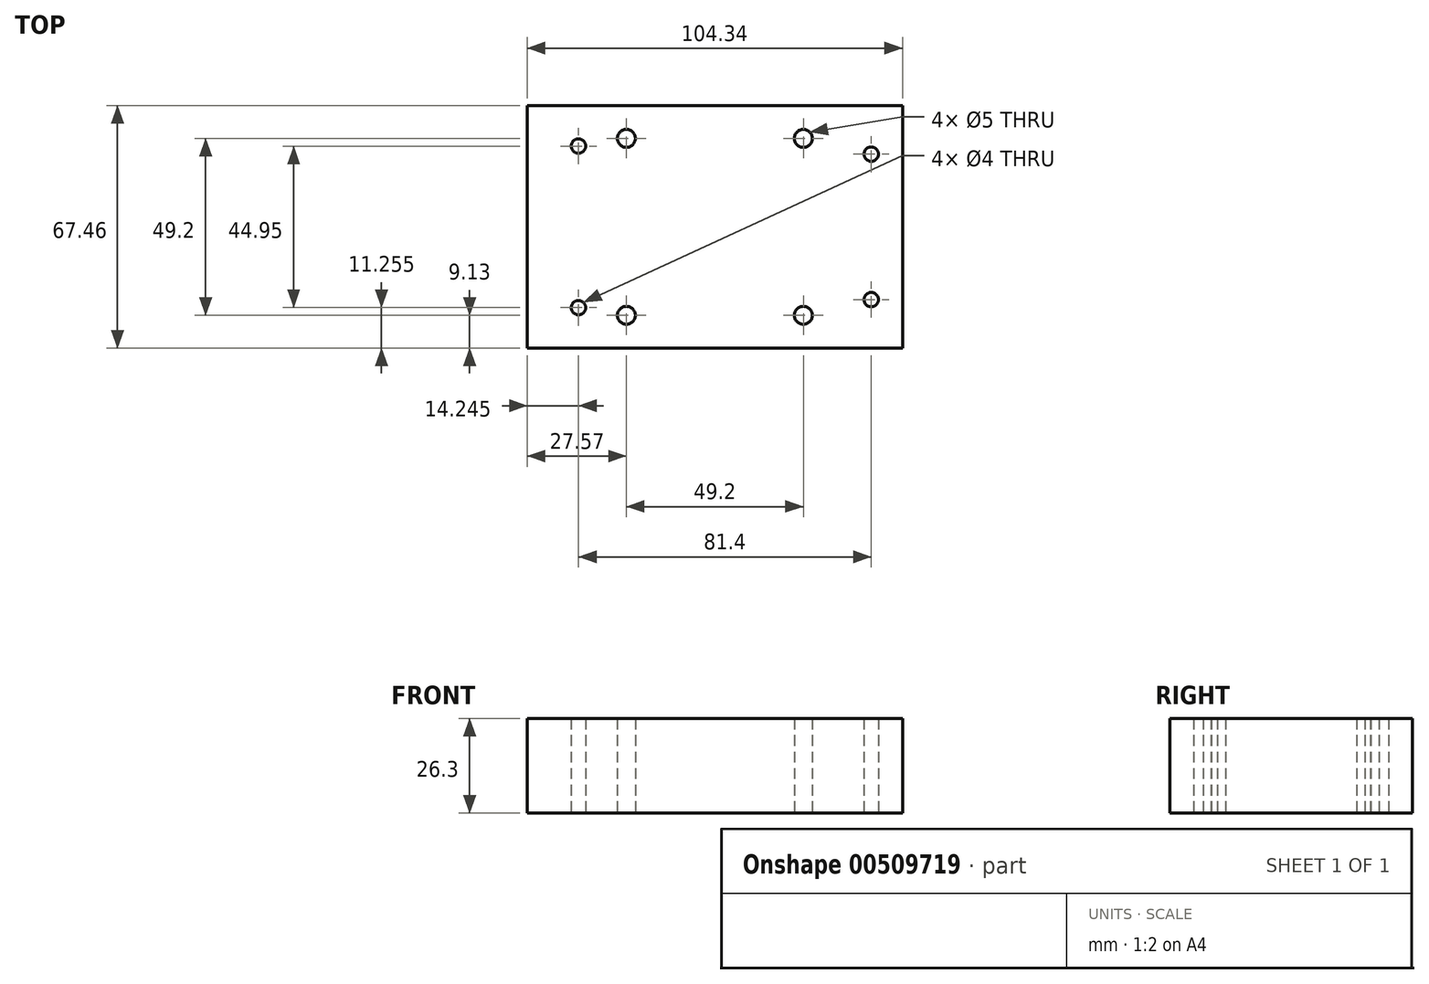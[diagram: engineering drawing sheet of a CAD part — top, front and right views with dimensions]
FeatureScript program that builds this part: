
annotation { "Feature Type Name" : "Feature", "Feature Type Description" : "" }
export const myFeature = defineFeature(function(context is Context, id is Id, definition is map)
    precondition{}
    {
        {
            var Q0;
            Q0=qCreatedBy(makeId("Top.planeOp"),FACE);
            var sketch = newSketch(context, id + "F0", { "sketchPlane" : qUnion([Q0])});
            skLineSegment(sketch, "E0.bottom", {"start": v(52.17, -33.73) * mm, "end": v(-52.17, -33.73) * mm});
            skLineSegment(sketch, "E0.top", {"start": v(52.17, 33.73) * mm, "end": v(-52.18, 33.73) * mm});
            skLineSegment(sketch, "E0.left", {"start": v(52.17, -33.73) * mm, "end": v(52.17, 33.73) * mm});
            skLineSegment(sketch, "E0.right", {"start": v(-52.17, -33.73) * mm, "end": v(-52.18, 33.73) * mm});
            skPoint(sketch, "E0.middle", {"position": v(0, 0) * mm});
            skSolve(sketch);
        }
        {
            var Q0;
            Q0 = qSketchRegion(id + "F0", true);
            extrude(context, id + "F1", {"entities" : qUnion([Q0]), "depth" : 26.3 * mm});
        }
        {
            var Q0;
            Q0=qCreatedBy(makeId("Top.planeOp"),FACE);
            var sketch = newSketch(context, id + "F2", { "sketchPlane" : qUnion([Q0])});
            skLineSegment(sketch, "E1.bottom", {"start": v(38.65, -38.65) * mm, "end": v(-38.65, -38.65) * mm});
            skLineSegment(sketch, "E1.top", {"start": v(38.65, 38.65) * mm, "end": v(-38.65, 38.65) * mm});
            skLineSegment(sketch, "E1.left", {"start": v(38.65, -38.65) * mm, "end": v(38.65, 38.65) * mm});
            skLineSegment(sketch, "E1.right", {"start": v(-38.65, -38.65) * mm, "end": v(-38.65, 38.65) * mm});
            skPoint(sketch, "E1.middle", {"position": v(0, 0) * mm});
            skCircle(sketch, "E2", {"center": v(24.6, 24.6) * mm, "radius": 2.5 * mm});
            skCircle(sketch, "E3", {"center": v(24.6, -24.6) * mm, "radius": 2.5 * mm});
            skCircle(sketch, "E4", {"center": v(-24.6, -24.6) * mm, "radius": 2.5 * mm});
            skCircle(sketch, "E5", {"center": v(-24.6, 24.6) * mm, "radius": 2.5 * mm});
            skSolve(sketch);
        }
        {
            var Q0;
            Q0=makeQuery(id+"F2.imprint","IMPRINT",FACE,{"disambiguationData":[TD([[makeQuery(id+"F2.imprint","IMPRINT",EDGE,{"derivedFrom":sQuery(id+"F2.wireOp",EDGE,"E5")}),1.0]])]});
            var Q1;
            Q1=makeQuery(id+"F2.imprint","IMPRINT",FACE,{"disambiguationData":[TD([[makeQuery(id+"F2.imprint","IMPRINT",EDGE,{"derivedFrom":sQuery(id+"F2.wireOp",EDGE,"E4")}),1.0]])]});
            var Q2;
            Q2=makeQuery(id+"F2.imprint","IMPRINT",FACE,{"disambiguationData":[TD([[makeQuery(id+"F2.imprint","IMPRINT",EDGE,{"derivedFrom":sQuery(id+"F2.wireOp",EDGE,"E3")}),1.0]])]});
            var Q3;
            Q3=makeQuery(id+"F2.imprint","IMPRINT",FACE,{"disambiguationData":[TD([[makeQuery(id+"F2.imprint","IMPRINT",EDGE,{"derivedFrom":sQuery(id+"F2.wireOp",EDGE,"E2")}),1.0]])]});
            var Q4;
            Q4=sQuery(id+"F2.wireOp",EDGE,"E4");
            var Q5;
            Q5=sQuery(id+"F2.wireOp",EDGE,"E5");
            var Q6;
            Q6=sQuery(id+"F2.wireOp",EDGE,"E2");
            var Q7;
            Q7=sQuery(id+"F2.wireOp",EDGE,"E3");
            extrude(context, id + "F3", {"entities" : qUnion([Q0, Q1, Q2, Q3]), "operationType" : NewBodyOperationType.REMOVE, "surfaceEntities" : qUnion([Q4, Q5, Q6, Q7]), "endBound" : BoundingType.THROUGH_ALL, "depth" : 25 * mm});
        }
        {
            var Q0;
            Q0=qCreatedBy(makeId("Top.planeOp"),FACE);
            var sketch = newSketch(context, id + "F4", { "sketchPlane" : qUnion([Q0])});
            skCircle(sketch, "E6", {"center": v(43.47, 20.23) * mm, "radius": 2 * mm});
            skCircle(sketch, "E7", {"center": v(43.47, -20.23) * mm, "radius": 2 * mm});
            skCircle(sketch, "E8", {"center": v(-37.93, 22.48) * mm, "radius": 2 * mm});
            skCircle(sketch, "E9", {"center": v(-37.93, -22.48) * mm, "radius": 2 * mm});
            skSolve(sketch);
        }
        {
            var Q0;
            Q0 = qSketchRegion(id + "F4", true);
            extrude(context, id + "F5", {"entities" : qUnion([Q0]), "operationType" : NewBodyOperationType.REMOVE, "depth" : 70.6 * mm});
        }
    });
